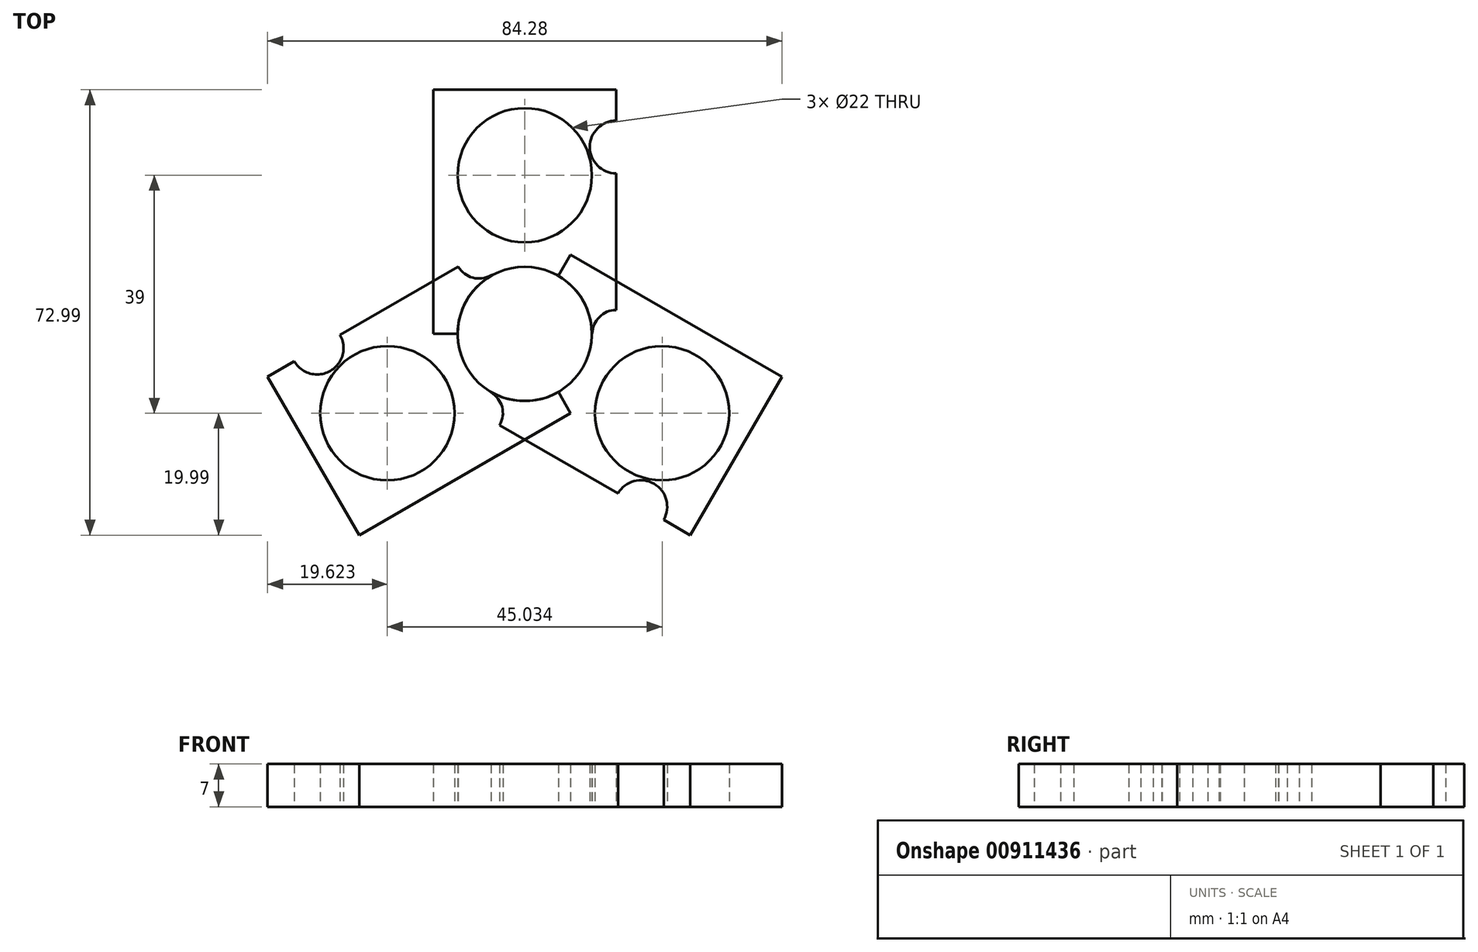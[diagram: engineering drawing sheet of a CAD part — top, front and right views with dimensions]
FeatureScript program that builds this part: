
annotation { "Feature Type Name" : "Feature", "Feature Type Description" : "" }
export const myFeature = defineFeature(function(context is Context, id is Id, definition is map)
    precondition{}
    {
        {
            var Q0;
            Q0=qCreatedBy(makeId("Top.planeOp"),FACE);
            var sketch = newSketch(context, id + "F0", { "sketchPlane" : qUnion([Q0])});
            skCircle(sketch, "E0", {"center": v(0, 0) * mm, "radius": 11 * mm});
            skLineSegment(sketch, "E1.bottom", {"start": v(0, 0) * mm, "end": v(15, 0) * mm});
            skLineSegment(sketch, "E1.top", {"start": v(0, 40) * mm, "end": v(15, 40) * mm});
            skLineSegment(sketch, "E1.left", {"start": v(0, 0) * mm, "end": v(0, 40) * mm});
            skLineSegment(sketch, "E1.right", {"start": v(15, 0) * mm, "end": v(15, 40) * mm});
            skLineSegment(sketch, "E2.bottom", {"start": v(0, 0) * mm, "end": v(-15, 0) * mm});
            skLineSegment(sketch, "E2.top", {"start": v(0, 40) * mm, "end": v(-15, 40) * mm});
            skLineSegment(sketch, "E2.right", {"start": v(-15, 0) * mm, "end": v(-15, 40) * mm});
            skLineSegment(sketch, "E3", {"start": v(0, 40) * mm, "end": v(0, 26) * mm});
            skCircle(sketch, "E4", {"center": v(0, 26) * mm, "radius": 11 * mm});
            skCircle(sketch, "E5", {"center": v(15, 30.63) * mm, "radius": 4.32 * mm});
            skCircle(sketch, "E6", {"center": v(15, 0) * mm, "radius": 3.92 * mm});
            skSolve(sketch);
        }
        {
            var Q0;
            {var subQ9=sQuery(id+"F0.wireOp",EDGE,"E1.top");Q0=makeQuery(id+"F0.imprint","IMPRINT",FACE,{"disambiguationData":[TD([[makeQuery(id+"F0.imprint","IMPRINT",EDGE,{"derivedFrom":subQ9}),-1.0]])]});}
            var Q1;
            {var subQ0=sQuery(id+"F0.wireOp",EDGE,"E2.top");Q1=makeQuery(id+"F0.imprint","IMPRINT",FACE,{"disambiguationData":[TD([[makeQuery(id+"F0.imprint","IMPRINT",EDGE,{"derivedFrom":subQ0}),1.0]])]});}
            extrude(context, id + "F1", {"entities" : qUnion([Q0, Q1]), "depth" : 7 * mm, "offsetDistance" : 25 * mm});
        }
        {
            var Q0;
            Q0=qCreatedBy(makeId("Front.planeOp"),FACE);
            var sketch = newSketch(context, id + "F2", { "sketchPlane" : qUnion([Q0])});
            skLineSegment(sketch, "E7", {"start": v(0, 0) * mm, "end": v(0, 45.82) * mm});
            skSolve(sketch);
        }
        {
            var Q0;
            Q0=makeQuery(id+"F1.opExtrude","SWEPT_BODY",BODY,{"disambiguationData":[OSD([sQuery(id+"F0.wireOp",EDGE,"E0"),sQuery(id+"F0.wireOp",EDGE,"E1.bottom"),sQuery(id+"F0.wireOp",EDGE,"E1.top"),sQuery(id+"F0.wireOp",EDGE,"E1.right"),sQuery(id+"F0.wireOp",EDGE,"E2.bottom"),sQuery(id+"F0.wireOp",EDGE,"E2.top"),sQuery(id+"F0.wireOp",EDGE,"E2.right"),sQuery(id+"F0.wireOp",EDGE,"E4")])]});
            var Q1;
            Q1=sQuery(id+"F2.wireOp",EDGE,"E7");
            transform(context, id + "F3", {"entities" : qUnion([Q0]), "transformType" : TransformType.ROTATION, "transformAxis" : qUnion([Q1]), "angle" : 120 * degree, "makeCopy" : false});
        }
        {
            var Q0;
            Q0=makeQuery(id+"F1.opExtrude","SWEPT_BODY",BODY,{"disambiguationData":[OSD([sQuery(id+"F0.wireOp",EDGE,"E0"),sQuery(id+"F0.wireOp",EDGE,"E1.bottom"),sQuery(id+"F0.wireOp",EDGE,"E1.top"),sQuery(id+"F0.wireOp",EDGE,"E1.right"),sQuery(id+"F0.wireOp",EDGE,"E2.bottom"),sQuery(id+"F0.wireOp",EDGE,"E2.top"),sQuery(id+"F0.wireOp",EDGE,"E2.right"),sQuery(id+"F0.wireOp",EDGE,"E4")])]});
            var Q1;
            Q1=sQuery(id+"F2.wireOp",EDGE,"E7");
            transform(context, id + "F4", {"entities" : qUnion([Q0]), "transformType" : TransformType.ROTATION, "transformAxis" : qUnion([Q1]), "angle" : 120 * degree, "makeCopy" : true});
        }
        {
            var Q0;
            Q0=makeQuery(id+"F4.opPattern","COPY",BODY,{"derivedFrom":makeQuery(id+"F1.opExtrude","SWEPT_BODY",BODY,{"disambiguationData":[OSD([sQuery(id+"F0.wireOp",EDGE,"E0"),sQuery(id+"F0.wireOp",EDGE,"E1.bottom"),sQuery(id+"F0.wireOp",EDGE,"E1.top"),sQuery(id+"F0.wireOp",EDGE,"E1.right"),sQuery(id+"F0.wireOp",EDGE,"E2.bottom"),sQuery(id+"F0.wireOp",EDGE,"E2.top"),sQuery(id+"F0.wireOp",EDGE,"E2.right"),sQuery(id+"F0.wireOp",EDGE,"E4")])]}),"instanceName":"1"});
            var Q1;
            Q1=sQuery(id+"F2.wireOp",EDGE,"E7");
            transform(context, id + "F5", {"entities" : qUnion([Q0]), "transformType" : TransformType.ROTATION, "transformAxis" : qUnion([Q1]), "angle" : 120 * degree, "makeCopy" : true});
        }
    });
